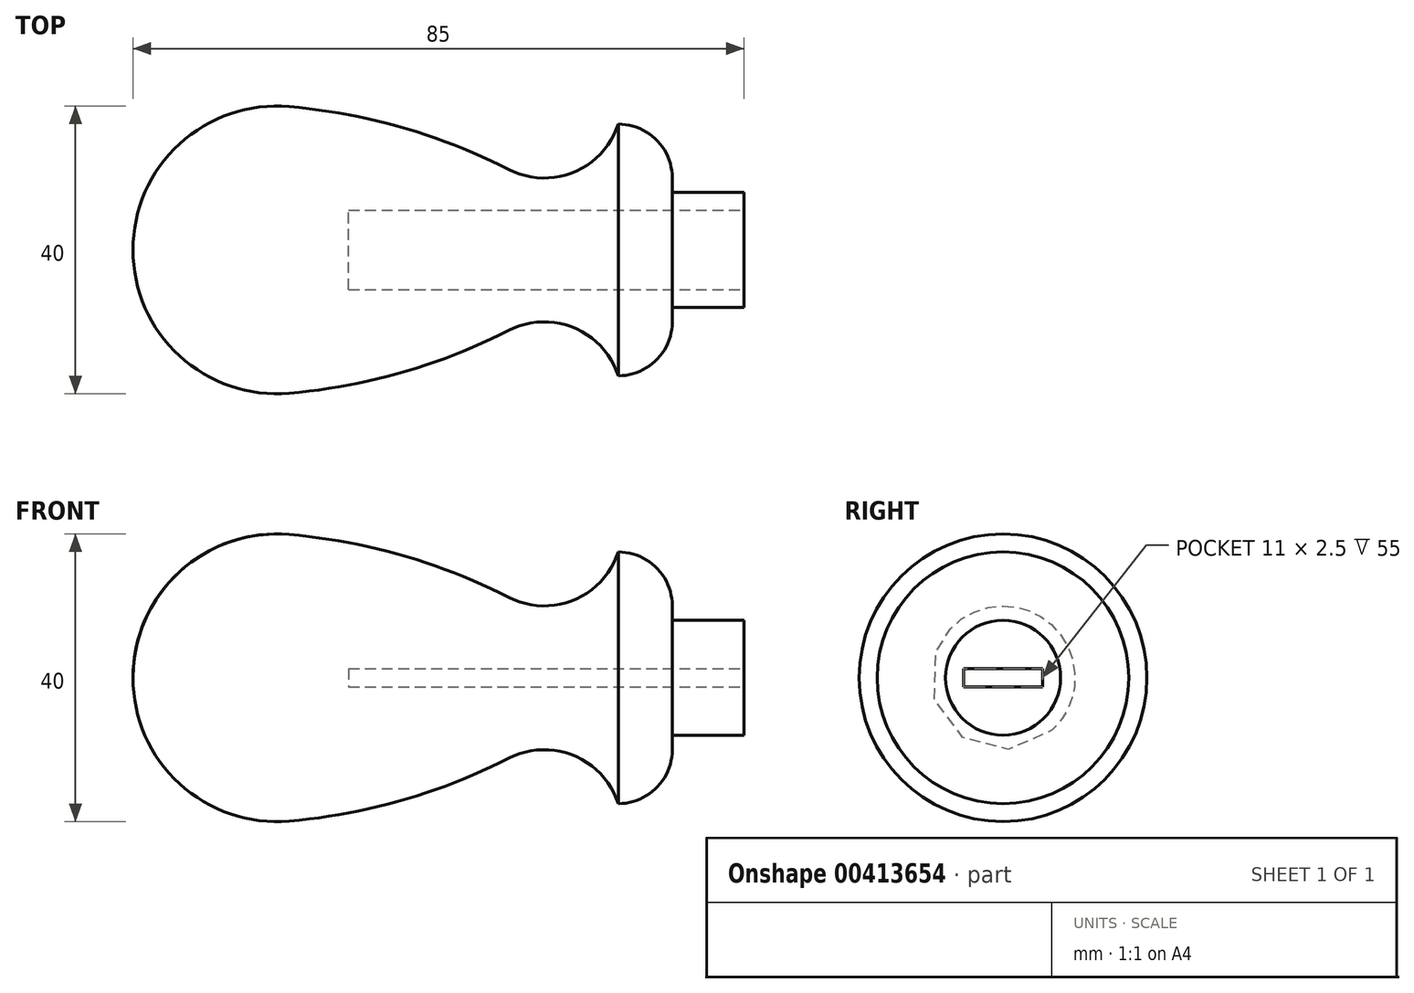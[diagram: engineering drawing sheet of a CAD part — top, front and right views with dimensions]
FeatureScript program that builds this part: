
annotation { "Feature Type Name" : "Feature", "Feature Type Description" : "" }
export const myFeature = defineFeature(function(context is Context, id is Id, definition is map)
    precondition{}
    {
        {
            var Q0;
            Q0=qCreatedBy(makeId("Front.planeOp"),FACE);
            var sketch = newSketch(context, id + "F0", { "sketchPlane" : qUnion([Q0])});
            skArc(sketch, "E0", {"start": v(1.73, 19.93) * mm, "mid": v(-13.52, 14.74) * mm, "end": v(-20, 0) * mm});
            skLineSegment(sketch, "E1", {"start": v(0, 0) * mm, "end": v(65, 0) * mm});
            skLineSegment(sketch, "E2", {"start": v(0, 0) * mm, "end": v(-20, 0) * mm, "construction": true});
            skLineSegment(sketch, "E3", {"start": v(65, 0) * mm, "end": v(65, 8) * mm});
            skLineSegment(sketch, "E4", {"start": v(65, 8) * mm, "end": v(55, 8) * mm});
            skLineSegment(sketch, "E5", {"start": v(55, 8) * mm, "end": v(55, 10) * mm});
            skArc(sketch, "E6", {"start": v(55, 10) * mm, "mid": v(52.8, 15.3) * mm, "end": v(47.5, 17.5) * mm});
            skArc(sketch, "E7", {"start": v(1.73, 19.93) * mm, "mid": v(17.42, 17.03) * mm, "end": v(32.26, 11.18) * mm});
            skArc(sketch, "E8", {"start": v(47.5, 17.5) * mm, "mid": v(41.34, 10.83) * mm, "end": v(32.26, 11.18) * mm});
            skLineSegment(sketch, "E9", {"start": v(-20, 0) * mm, "end": v(0, 0) * mm});
            skSolve(sketch);
        }
        {
            var Q0;
            Q0=makeQuery(id+"F0.imprint","IMPRINT",FACE,{"disambiguationData":[TD([[makeQuery(id+"F0.imprint","IMPRINT",EDGE,{"derivedFrom":sQuery(id+"F0.wireOp",EDGE,"E0")}),1.0]])]});
            var Q1;
            Q1=sQuery(id+"F0.wireOp",EDGE,"E0");
            var Q2;
            Q2=sQuery(id+"F0.wireOp",EDGE,"E7");
            var Q3;
            Q3=sQuery(id+"F0.wireOp",EDGE,"E8");
            var Q4;
            Q4=sQuery(id+"F0.wireOp",EDGE,"E6");
            var Q5;
            Q5=sQuery(id+"F0.wireOp",EDGE,"E5");
            var Q6;
            Q6=sQuery(id+"F0.wireOp",EDGE,"E4");
            var Q7;
            Q7=sQuery(id+"F0.wireOp",EDGE,"E3");
            var Q8;
            Q8=sQuery(id+"F0.wireOp",EDGE,"E1");
            revolve(context, id + "F1", {"entities" : qUnion([Q0]), "surfaceEntities" : qUnion([Q1, Q2, Q3, Q4, Q5, Q6, Q7]), "axis" : qUnion([Q8]), "revolveType" : RevolveType.FULL});
        }
        {
            var Q0;
            Q0=makeQuery(id+"F1.opRevolve","SWEPT_FACE",FACE,{"disambiguationData":[OSD([sQuery(id+"F0.wireOp",EDGE,"E3")])]});
            var sketch = newSketch(context, id + "F2", { "sketchPlane" : qUnion([Q0])});
            skLineSegment(sketch, "E10.bottom", {"start": v(-5.5, 1.25) * mm, "end": v(5.5, 1.25) * mm});
            skLineSegment(sketch, "E10.top", {"start": v(-5.5, -1.25) * mm, "end": v(5.5, -1.25) * mm});
            skLineSegment(sketch, "E10.left", {"start": v(-5.5, 1.25) * mm, "end": v(-5.5, -1.25) * mm});
            skLineSegment(sketch, "E10.right", {"start": v(5.5, 1.25) * mm, "end": v(5.5, -1.25) * mm});
            skPoint(sketch, "E10.middle", {"position": v(0, 0) * mm});
            skSolve(sketch);
        }
        {
            var Q0;
            Q0=makeQuery(id+"F2.imprint","IMPRINT",FACE,{"disambiguationData":[TD([[makeQuery(id+"F2.imprint","IMPRINT",EDGE,{"derivedFrom":sQuery(id+"F2.wireOp",EDGE,"E10.bottom")}),-1.0]])]});
            extrude(context, id + "F3", {"entities" : qUnion([Q0]), "operationType" : NewBodyOperationType.REMOVE, "oppositeDirection" : true, "depth" : 55 * mm});
        }
    });
